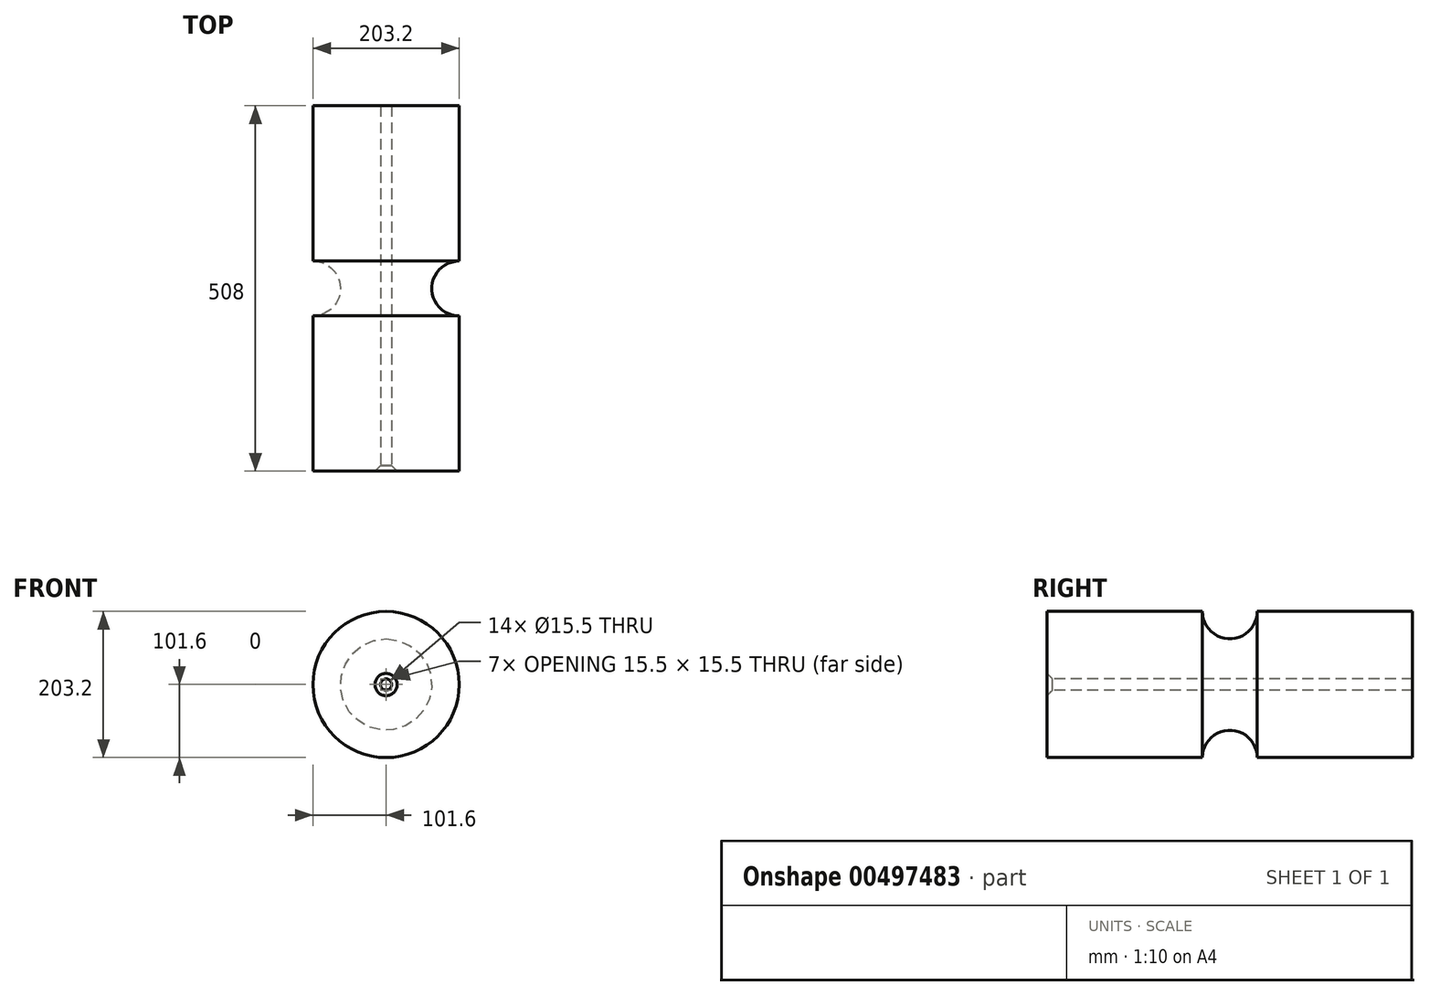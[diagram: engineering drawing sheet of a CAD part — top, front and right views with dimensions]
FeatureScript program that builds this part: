
annotation { "Feature Type Name" : "Feature", "Feature Type Description" : "" }
export const myFeature = defineFeature(function(context is Context, id is Id, definition is map)
    precondition{}
    {
        {
            var Q0;
            Q0=qCreatedBy(makeId("Top.planeOp"),FACE);
            var sketch = newSketch(context, id + "F0", { "sketchPlane" : qUnion([Q0])});
            skLineSegment(sketch, "E0", {"start": v(0, 254) * mm, "end": v(0, -254) * mm});
            skPoint(sketch, "E1", {"position": v(0, 0) * mm});
            skLineSegment(sketch, "E2", {"start": v(0, 254) * mm, "end": v(101.6, 254) * mm});
            skLineSegment(sketch, "E3", {"start": v(101.6, 254) * mm, "end": v(101.6, 38.1) * mm});
            skArc(sketch, "E4", {"start": v(101.6, 38.1) * mm, "mid": v(63.5, 0) * mm, "end": v(101.6, -38.1) * mm});
            skLineSegment(sketch, "E5", {"start": v(0, -254) * mm, "end": v(101.6, -254) * mm});
            skLineSegment(sketch, "E6", {"start": v(101.6, -254) * mm, "end": v(101.6, -38.1) * mm});
            skSolve(sketch);
        }
        {
            var Q0;
            Q0 = qSketchRegion(id + "F0", true);
            var Q1;
            Q1=sQuery(id+"F0.wireOp",EDGE,"E0");
            revolve(context, id + "F1", {"entities" : qUnion([Q0]), "axis" : qUnion([Q1]), "revolveType" : RevolveType.FULL});
        }
        {
            var Q0;
            Q0=makeQuery(id+"F1.opRevolve","SWEPT_FACE",FACE,{"disambiguationData":[OSD([sQuery(id+"F0.wireOp",EDGE,"E5")])]});
            var sketch = newSketch(context, id + "F2", { "sketchPlane" : qUnion([Q0])});
            skPoint(sketch, "E7", {"position": v(0, 0) * mm});
            skSolve(sketch);
        }
        {
            var Q0;
            Q0=sQuery(id+"F2.wireOp",VERTEX,"E7");
            var Q1;
            Q1=makeQuery(id+"F1.opRevolve","SWEPT_BODY",BODY,{"disambiguationData":[OSD([sQuery(id+"F0.wireOp",EDGE,"E0"),sQuery(id+"F0.wireOp",EDGE,"E2"),sQuery(id+"F0.wireOp",EDGE,"E3"),sQuery(id+"F0.wireOp",EDGE,"E4"),sQuery(id+"F0.wireOp",EDGE,"E5"),sQuery(id+"F0.wireOp",EDGE,"E6")])]});
            hole(context, id + "F3", {"style" : HoleStyle.C_SINK, "endStyle" : HoleEndStyle.THROUGH, "standardTappedOrClearance" : lookupTablePath({ "standard" : "ISO", "fit" : "Normal", "size" : "M14", "type" : "Clearance" }), "standardBlindInLast" : lookupTablePath({ "fit" : "Standard", "standard" : "ISO", "size" : "M14", "type" : "Clearance" }), "holeDiameter" : 15.5 * mm, "cSinkDiameter" : 30.8 * mm, "cSinkAngle" : 90 * degree, "isTappedThrough" : true, "tappedDepth" : 12 * mm, "tapClearance" : 3, "startFromSketch" : true, "locations" : qUnion([Q0]), "scope" : qUnion([Q1])});
        }
    });
